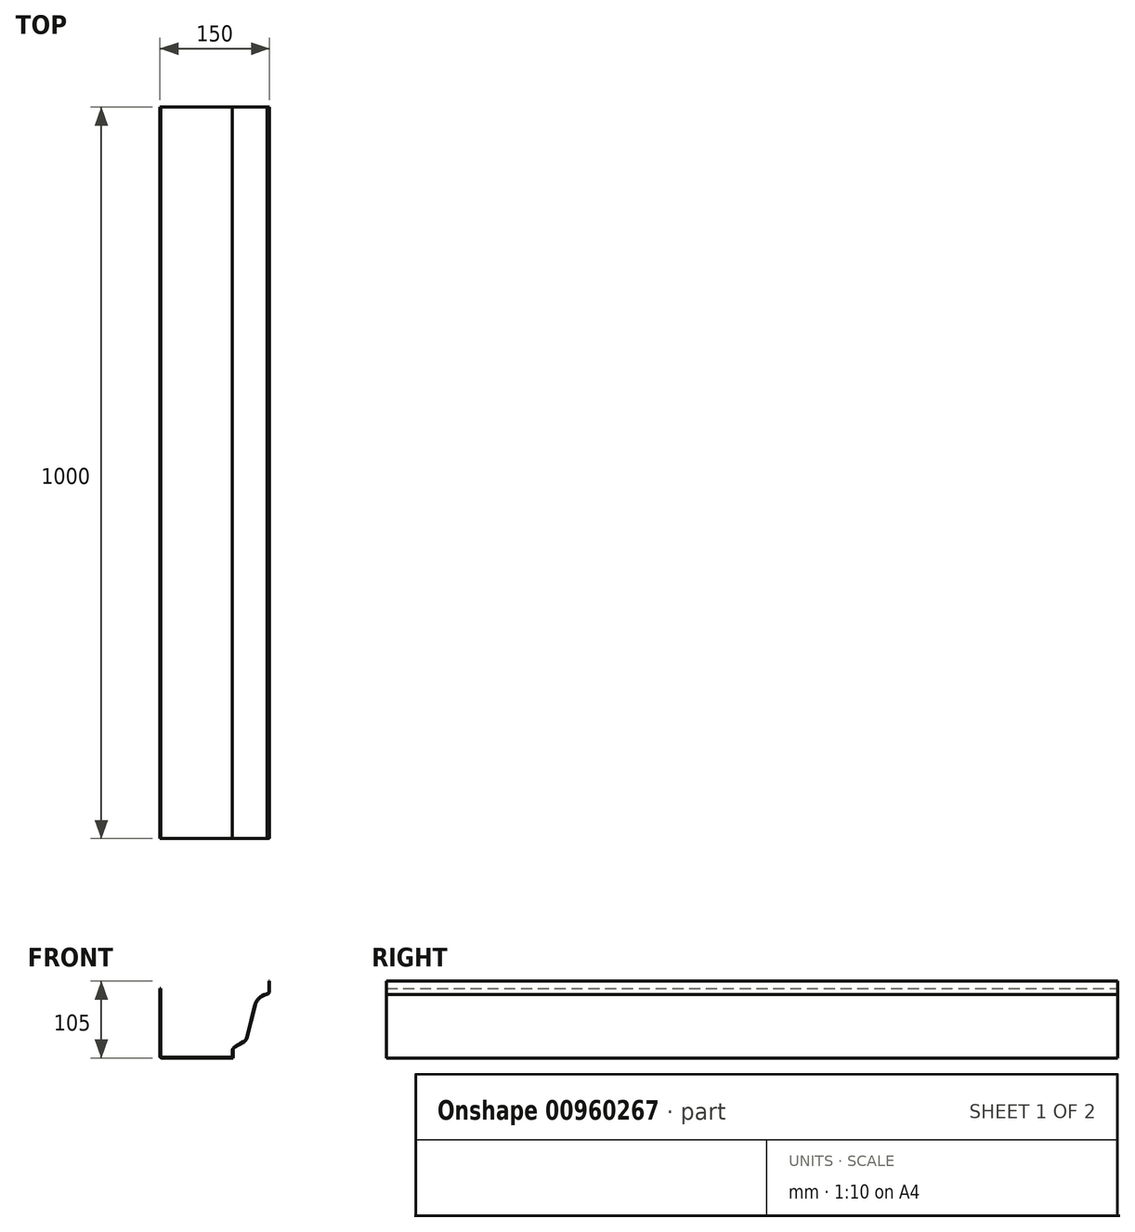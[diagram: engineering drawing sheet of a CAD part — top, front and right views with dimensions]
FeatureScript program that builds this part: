
annotation { "Feature Type Name" : "Feature", "Feature Type Description" : "" }
export const myFeature = defineFeature(function(context is Context, id is Id, definition is map)
    precondition{}
    {
        {
            var Q0;
            Q0=qCreatedBy(makeId("Front.planeOp"),FACE);
            var sketch = newSketch(context, id + "F0", { "sketchPlane" : qUnion([Q0])});
            skLineSegment(sketch, "E0.right", {"start": v(75, 52.5) * mm, "end": v(75, 38.91) * mm});
            skPoint(sketch, "E0.middle", {"position": v(0, 0) * mm});
            skArc(sketch, "E1", {"start": v(71.93, 34.26) * mm, "mid": v(61.54, 29.3) * mm, "end": v(55.61, 19.41) * mm});
            skArc(sketch, "E2", {"start": v(39.92, -30.84) * mm, "mid": v(42.75, -28.3) * mm, "end": v(44.39, -24.88) * mm});
            skArc(sketch, "E3", {"start": v(27.46, -38.2) * mm, "mid": v(25.66, -40.02) * mm, "end": v(25, -42.5) * mm});
            skLineSegment(sketch, "E4", {"start": v(27.46, -38.2) * mm, "end": v(39.92, -30.84) * mm});
            skLineSegment(sketch, "E5", {"start": v(44.39, -24.88) * mm, "end": v(55.61, 19.41) * mm});
            skArc(sketch, "E6", {"start": v(71.93, 34.26) * mm, "mid": v(74.17, 36.12) * mm, "end": v(75, 38.91) * mm});
            skPoint(sketch, "E7.orphan", {"position": v(-75, -52.5) * mm});
            skPoint(sketch, "E8.right.start.orphan", {"position": v(25, -52.5) * mm});
            skLineSegment(sketch, "E9", {"start": v(-73, -52.5) * mm, "end": v(25, -52.5) * mm});
            skLineSegment(sketch, "E10", {"start": v(25, -52.5) * mm, "end": v(25, -42.5) * mm});
            skLineSegment(sketch, "E11", {"start": v(-75, -50.5) * mm, "end": v(-75, 42.5) * mm});
            skLineSegment(sketch, "E12", {"start": v(-74, 42.5) * mm, "end": v(-74, -50.5) * mm});
            skLineSegment(sketch, "E13", {"start": v(-73, -51.5) * mm, "end": v(24, -51.5) * mm});
            skLineSegment(sketch, "E14", {"start": v(24, -51.5) * mm, "end": v(24, -42.5) * mm});
            skLineSegment(sketch, "E15", {"start": v(26.95, -37.33) * mm, "end": v(39.41, -29.98) * mm});
            skLineSegment(sketch, "E16", {"start": v(74, 52.5) * mm, "end": v(74, 38.88) * mm});
            skLineSegment(sketch, "E17", {"start": v(74, 52.5) * mm, "end": v(75, 52.5) * mm});
            skArc(sketch, "E18.trimOffspring", {"start": v(26.95, -37.33) * mm, "mid": v(24.79, -39.52) * mm, "end": v(24, -42.5) * mm});
            skArc(sketch, "E19", {"start": v(39.41, -29.98) * mm, "mid": v(41.95, -27.7) * mm, "end": v(43.42, -24.63) * mm});
            skArc(sketch, "E20", {"start": v(71.65, 35.23) * mm, "mid": v(60.82, 29.99) * mm, "end": v(54.64, 19.66) * mm});
            skLineSegment(sketch, "E21", {"start": v(54.64, 19.66) * mm, "end": v(43.42, -24.63) * mm});
            skArc(sketch, "E22", {"start": v(71.65, 35.23) * mm, "mid": v(73.36, 36.7) * mm, "end": v(74, 38.88) * mm});
            skPoint(sketch, "E23", {"position": v(-73, -50.5) * mm});
            skArc(sketch, "E24", {"start": v(-74, -50.5) * mm, "mid": v(-73.7, -51.2) * mm, "end": v(-73, -51.5) * mm});
            skArc(sketch, "E25", {"start": v(-75, -50.5) * mm, "mid": v(-74.41, -51.91) * mm, "end": v(-73, -52.5) * mm});
            skPoint(sketch, "E26.orphan", {"position": v(-74, -51.5) * mm});
            skLineSegment(sketch, "E27", {"start": v(-75, 42.5) * mm, "end": v(-74, 42.5) * mm});
            skSolve(sketch);
        }
        {
            var Q0;
            Q0=qSketchRegion(id+"F0",true);
            extrude(context, id + "F1", {"entities" : qUnion([Q0]), "depth" : 1000 * mm, "offsetDistance" : 25 * mm});
        }
    });
